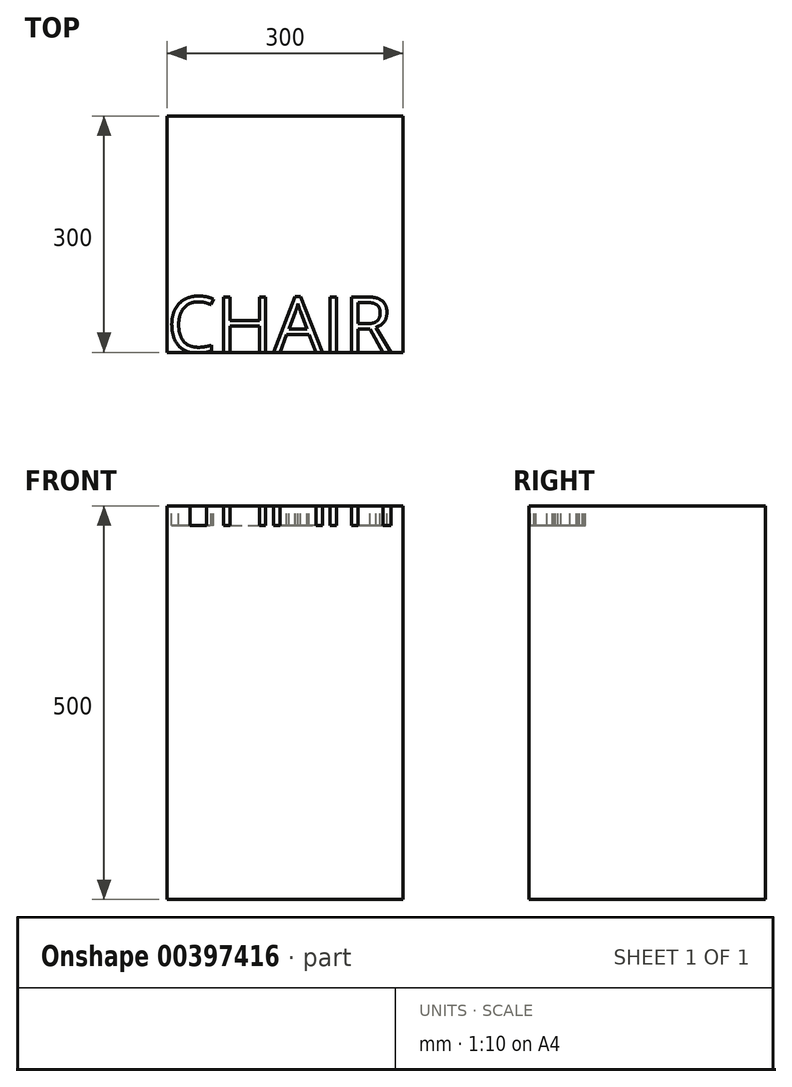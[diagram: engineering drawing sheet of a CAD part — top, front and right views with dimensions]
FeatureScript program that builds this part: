
annotation { "Feature Type Name" : "Feature", "Feature Type Description" : "" }
export const myFeature = defineFeature(function(context is Context, id is Id, definition is map)
    precondition{}
    {
        {
            var Q0;
            Q0=qCreatedBy(makeId("Top.planeOp"),FACE);
            var sketch = newSketch(context, id + "F0", { "sketchPlane" : qUnion([Q0])});
            skLineSegment(sketch, "E0.bottom", {"start": v(150, -150) * mm, "end": v(-150, -150) * mm});
            skLineSegment(sketch, "E0.top", {"start": v(150, 150) * mm, "end": v(-150, 150) * mm});
            skLineSegment(sketch, "E0.left", {"start": v(150, -150) * mm, "end": v(150, 150) * mm});
            skLineSegment(sketch, "E0.right", {"start": v(-150, -150) * mm, "end": v(-150, 150) * mm});
            skPoint(sketch, "E0.middle", {"position": v(0, 0) * mm});
            skSolve(sketch);
        }
        {
            var Q0;
            Q0 = qSketchRegion(id + "F0", true);
            extrude(context, id + "F1", {"entities" : qUnion([Q0]), "depth" : 500 * mm});
        }
        {
            var Q0;
            Q0=makeQuery(id+"F1.opExtrude","CAP_FACE",FACE,{"disambiguationData":[OSD([sQuery(id+"F0.wireOp",EDGE,"E0.bottom"),sQuery(id+"F0.wireOp",EDGE,"E0.top"),sQuery(id+"F0.wireOp",EDGE,"E0.left"),sQuery(id+"F0.wireOp",EDGE,"E0.right")])],"isStart":false});
            var sketch = newSketch(context, id + "F2", { "sketchPlane" : qUnion([Q0])});
            skText(sketch, "E1", { "text": "CHAIR", "fontName": "OpenSans-Regular.ttf"});
            const initialGuessF2  = {"E1": [-0.15, -0.15, 1, 0, 0.07103]};
            skSetInitialGuess(sketch, initialGuessF2);
            skSolve(sketch);
        }
        {
            var Q0;
            Q0 = qSketchRegion(id + "F2", true);
            extrude(context, id + "F3", {"entities" : qUnion([Q0]), "operationType" : NewBodyOperationType.REMOVE, "oppositeDirection" : true, "depth" : 25 * mm});
        }
    });
